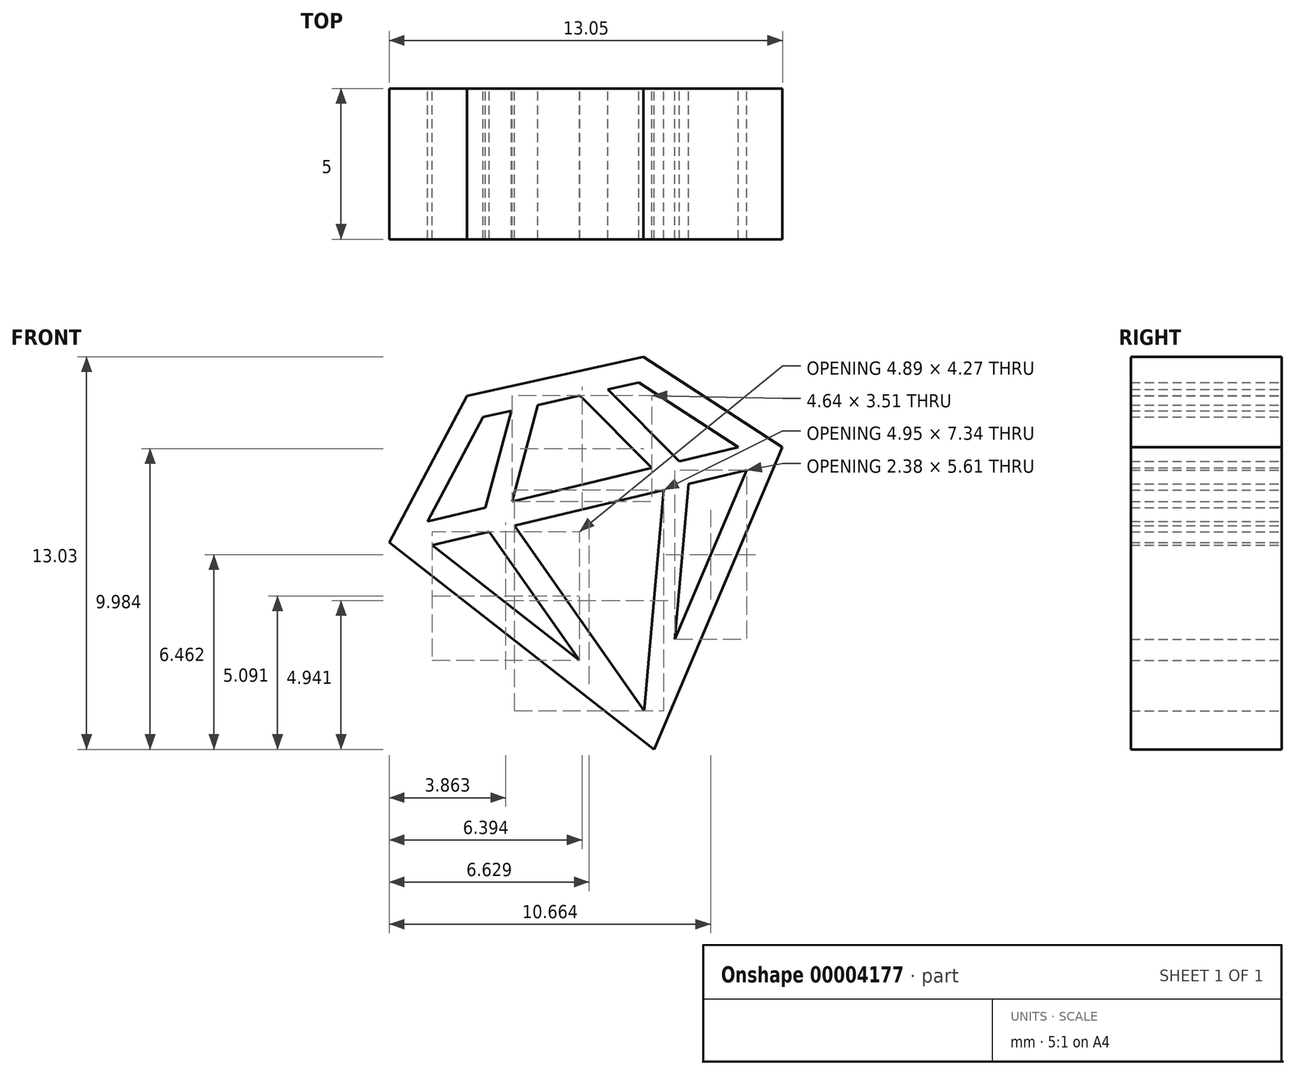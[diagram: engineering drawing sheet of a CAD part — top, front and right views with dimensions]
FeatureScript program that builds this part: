
annotation { "Feature Type Name" : "Feature", "Feature Type Description" : "" }
export const myFeature = defineFeature(function(context is Context, id is Id, definition is map)
    precondition{}
    {
        {
            var Q0;
            Q0=qCreatedBy(makeId("Front.planeOp"),FACE);
            var sketch = newSketch(context, id + "F0", { "sketchPlane" : qUnion([Q0])});
            skArc(sketch, "E0", {"start": v(4.57, 9.18) * mm, "mid": v(-6.31, -8.08) * mm, "end": v(7.8, 6.65) * mm});
            skCircle(sketch, "E1", {"center": v(0, 0) * mm, "radius": 9.25 * mm});
            skLineSegment(sketch, "E2", {"start": v(4.57, 9.18) * mm, "end": v(-1, 13.52) * mm});
            skLineSegment(sketch, "E3", {"start": v(-1, 13.52) * mm, "end": v(1.59, 18.38) * mm});
            skLineSegment(sketch, "E4", {"start": v(1.59, 18.38) * mm, "end": v(7.45, 19.68) * mm});
            skLineSegment(sketch, "E5", {"start": v(7.45, 19.68) * mm, "end": v(12.06, 16.68) * mm});
            skLineSegment(sketch, "E6", {"start": v(12.06, 16.68) * mm, "end": v(7.8, 6.65) * mm});
            skLineSegment(sketch, "E7", {"start": v(0, 0) * mm, "end": v(0, 26.5) * mm, "construction": true});
            skLineSegment(sketch, "E8", {"start": v(0, 0) * mm, "end": v(21.46, 0) * mm, "construction": true});
            skLineSegment(sketch, "E9.0", {"start": v(2.12, 17.68) * mm, "end": v(3.06, 17.88) * mm});
            skLineSegment(sketch, "E10.0", {"start": v(7.3, 18.82) * mm, "end": v(10.6, 16.68) * mm});
            skLineSegment(sketch, "E11.0", {"start": v(10.86, 15.92) * mm, "end": v(8.48, 10.3) * mm});
            skLineSegment(sketch, "E12.0", {"start": v(0.28, 14.2) * mm, "end": v(2.12, 17.68) * mm});
            skLineSegment(sketch, "E13.trimOffspring", {"start": v(5.32, 9.6) * mm, "end": v(0.43, 13.42) * mm});
            skLineSegment(sketch, "E14", {"start": v(0.03, 13.74) * mm, "end": v(11.06, 16.38) * mm, "construction": true});
            skLineSegment(sketch, "E15", {"start": v(0.28, 14.2) * mm, "end": v(2.2, 14.67) * mm});
            skLineSegment(sketch, "E16", {"start": v(3.06, 17.88) * mm, "end": v(2.2, 14.67) * mm});
            skLineSegment(sketch, "E17", {"start": v(2.33, 13.88) * mm, "end": v(5.32, 9.6) * mm});
            skLineSegment(sketch, "E18", {"start": v(4.7, 18.25) * mm, "end": v(7.47, 7.92) * mm, "construction": true});
            skLineSegment(sketch, "E19.0", {"start": v(3.16, 14.08) * mm, "end": v(7.47, 7.92) * mm});
            skLineSegment(sketch, "E19.1", {"start": v(3.94, 18.08) * mm, "end": v(3.08, 14.88) * mm});
            skLineSegment(sketch, "E20", {"start": v(2.33, 13.88) * mm, "end": v(2.08, 14.23) * mm, "construction": true});
            skLineSegment(sketch, "E21", {"start": v(2.08, 14.23) * mm, "end": v(2.2, 14.67) * mm, "construction": true});
            skLineSegment(sketch, "E22", {"start": v(6.26, 18.6) * mm, "end": v(8.64, 16.2) * mm});
            skLineSegment(sketch, "E23", {"start": v(8.93, 15.46) * mm, "end": v(8.48, 10.3) * mm});
            skLineSegment(sketch, "E24.0", {"start": v(8.11, 15.26) * mm, "end": v(7.47, 7.92) * mm});
            skLineSegment(sketch, "E24.1", {"start": v(5.33, 18.39) * mm, "end": v(7.73, 15.99) * mm});
            skLineSegment(sketch, "E25.trimOffspring", {"start": v(6.26, 18.6) * mm, "end": v(7.3, 18.82) * mm});
            skLineSegment(sketch, "E26.trimOffspring", {"start": v(3.94, 18.08) * mm, "end": v(5.33, 18.39) * mm});
            skLineSegment(sketch, "E27.trimOffspring", {"start": v(3.08, 14.88) * mm, "end": v(10.6, 16.68) * mm});
            skLineSegment(sketch, "E28", {"start": v(8.64, 16.2) * mm, "end": v(8.97, 15.88) * mm, "construction": true});
            skLineSegment(sketch, "E29", {"start": v(8.97, 15.88) * mm, "end": v(8.93, 15.46) * mm, "construction": true});
            skLineSegment(sketch, "E30", {"start": v(0.43, 13.42) * mm, "end": v(10.86, 15.92) * mm});
            skSolve(sketch);
        }
        {
            var Q0;
            Q0=qSketchRegion(id+"F0",true);
            extrude(context, id + "F1", {"entities" : qUnion([Q0]), "depth" : 5 * mm});
        }
        {
            var Q0;
            Q0=makeQuery(id+"F1.opExtrude","CAP_FACE",FACE,{"disambiguationData":[OSD([sQuery(id+"F0.wireOp",EDGE,"E0"),sQuery(id+"F0.wireOp",EDGE,"E1"),sQuery(id+"F0.wireOp",EDGE,"E2"),sQuery(id+"F0.wireOp",EDGE,"E3"),sQuery(id+"F0.wireOp",EDGE,"E4"),sQuery(id+"F0.wireOp",EDGE,"E5"),sQuery(id+"F0.wireOp",EDGE,"E6"),sQuery(id+"F0.wireOp",EDGE,"E9.0"),sQuery(id+"F0.wireOp",EDGE,"E10.0"),sQuery(id+"F0.wireOp",EDGE,"E11.0"),sQuery(id+"F0.wireOp",EDGE,"E12.0"),sQuery(id+"F0.wireOp",EDGE,"E13.trimOffspring"),sQuery(id+"F0.wireOp",EDGE,"E15"),sQuery(id+"F0.wireOp",EDGE,"E16"),sQuery(id+"F0.wireOp",EDGE,"E17"),sQuery(id+"F0.wireOp",EDGE,"E19.0"),sQuery(id+"F0.wireOp",EDGE,"E19.1"),sQuery(id+"F0.wireOp",EDGE,"E22"),sQuery(id+"F0.wireOp",EDGE,"E23"),sQuery(id+"F0.wireOp",EDGE,"E24.0"),sQuery(id+"F0.wireOp",EDGE,"E24.1"),sQuery(id+"F0.wireOp",EDGE,"E25.trimOffspring"),sQuery(id+"F0.wireOp",EDGE,"E26.trimOffspring"),sQuery(id+"F0.wireOp",EDGE,"E27.trimOffspring"),sQuery(id+"F0.wireOp",EDGE,"E30")])],"isStart":false});
            var sketch = newSketch(context, id + "F2", { "sketchPlane" : qUnion([Q0])});
            skLineSegment(sketch, "E31", {"start": v(4.57, 9.18) * mm, "end": v(7.8, 6.65) * mm});
            skArc(sketch, "E32.0", {"start": v(4.57, 9.18) * mm, "mid": v(-6.31, -8.08) * mm, "end": v(7.8, 6.65) * mm});
            skSolve(sketch);
        }
        {
            var Q0;
            {var subQ0=makeQuery(id+"F2.imprint","IMPRINT",EDGE,{"derivedFrom":makeQuery(id+"F1.opExtrude","CAP_EDGE",EDGE,{"disambiguationData":[OSD([sQuery(id+"F0.wireOp",EDGE,"E1")])],"isStart":false})});Q0=qUnion([makeQuery(id+"F2.imprint","IMPRINT",FACE,{"disambiguationData":[TD([[subQ0,1.0]])]}),makeQuery(id+"F2.imprint","IMPRINT",FACE,{"disambiguationData":[TD([[makeQuery(id+"F2.imprint","IMPRINT",EDGE,{"derivedFrom":sQuery(id+"F2.wireOp",EDGE,"E31")}),-1.0]])]})]);}
            extrude(context, id + "F3", {"entities" : qUnion([Q0]), "operationType" : NewBodyOperationType.REMOVE, "oppositeDirection" : true, "depth" : 25 * mm});
        }
    });
